# Revit family: Fire-Products_Sprinkler-Systems_YAMATO-PROTEC_SHS172002
name_source: partatom
category: スプリンクラ
revit_build: Autodesk Revit 2018 (Build: 20170223_1515(x64)
units: mm (PartAtom-declared; Revit-internal decimal feet)

## family parameters
パーツ タイプ = 標準
ホスト = 面
ロード時にボイドで切り取り = いいえ
丸型コネクタ寸法 = 直径を使用
共有 = いいえ
注釈の向きを維持 = いいえ
部屋計算ポイント = はい

## types (1)
- Fire-Products_Sprinkler-Systems_YAMATO-PROTEC_SHS172002
    Depth = 71  [stored 0.23294 ft]
    Height = 57  [stored 0.187008 ft]
    IfcExportAs = IfcFireSuppressionTerminalType
    IfcExportType = SPRINKLERDEFLECTOR
    OmniClassCode = 23-29 33 11 11 15
    ProductInformation = https://www.yamatoprotec.co.jp
    Uniclass2015Code = Pr_70_55_97_84
    Uniclass2015Title = Sprinkler heads
    Uniclass2015Version = Systems v1.9
    Width = 57  [stored 0.187008 ft]
    モデル = SHS172002
    仕様書バージョン = Version1.0
    企業コード = 580077214
    分類コード = 50903001200000
    呼称 = スプリンクラーヘッド
    形式 = 放水型
    既定の高さ = 1219
    積算_科目 = 9 消火設備
    製造元 = ヤマトプロテック株式会社
    説明 = 放水型スプリンクラーヘッド　SHS172002
    質量 = 0.25 kg

note: [stored X ft] marks values corroborated as IEEE doubles in the binary element streams (Revit-internal decimal feet)
